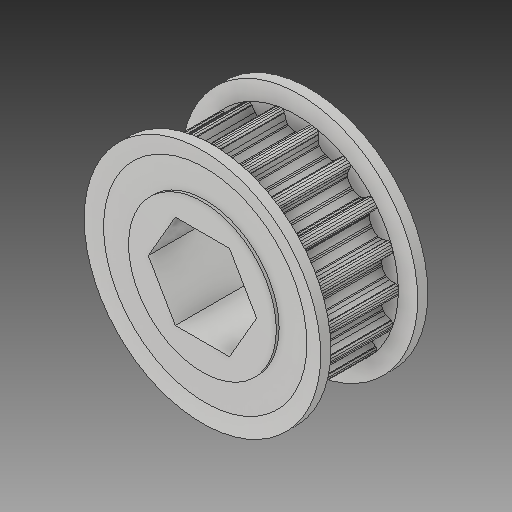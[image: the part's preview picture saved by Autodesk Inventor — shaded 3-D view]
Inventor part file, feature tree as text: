
AUTODESK INVENTOR PART (.ipt)
format: ipt  version: 2018 (Build 220112000, 112)  size: 547,840 bytes
history: native  units: in
note: dims shown in document units (in); Inventor stores cm internally (conversion verified against a paired STEP export)
features: mirror x1
ambient origin geometry x8: Origin, YZ Plane, XZ Plane, XY Plane, X Axis, Y Axis, Z Axis, Center Point
bodies: Solid1 (feature_tree)
feature tree (1):
  mirror  "Mirror1"
